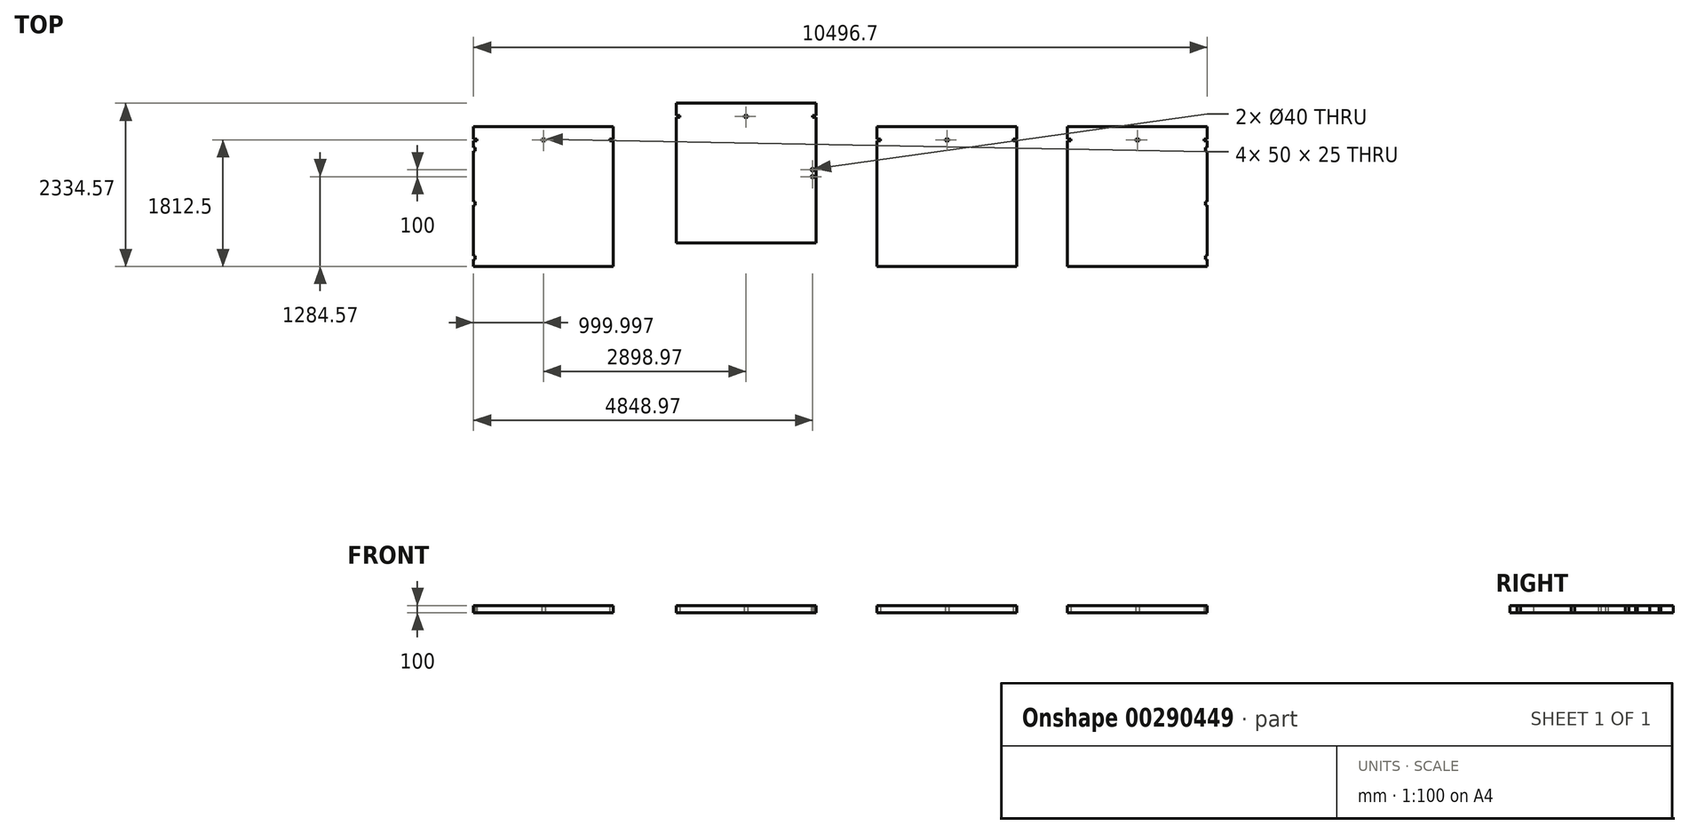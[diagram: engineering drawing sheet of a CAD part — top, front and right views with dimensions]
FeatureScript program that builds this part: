
annotation { "Feature Type Name" : "Feature", "Feature Type Description" : "" }
export const myFeature = defineFeature(function(context is Context, id is Id, definition is map)
    precondition{}
    {
        {
            var Q0;
            Q0=qCreatedBy(makeId("Top.planeOp"),FACE);
            var sketch = newSketch(context, id + "F0", { "sketchPlane" : qUnion([Q0])});
            skLineSegment(sketch, "E0.bottom", {"start": v(0, 0) * mm, "end": v(2000, 0) * mm});
            skLineSegment(sketch, "E0.top", {"start": v(0, -2000) * mm, "end": v(2000, -2000) * mm});
            skLineSegment(sketch, "E1.bottom", {"start": v(0, -200) * mm, "end": v(50, -200) * mm});
            skLineSegment(sketch, "E2.bottom", {"start": v(2000, -200) * mm, "end": v(1950, -200) * mm});
            skLineSegment(sketch, "E3.bottom", {"start": v(975, -200) * mm, "end": v(1025, -200) * mm});
            skLineSegment(sketch, "E4.bottom", {"start": v(50, -200) * mm, "end": v(0, -200) * mm});
            skLineSegment(sketch, "E4.top", {"start": v(50, -175) * mm, "end": v(0, -175) * mm});
            skLineSegment(sketch, "E4.left", {"start": v(50, -200) * mm, "end": v(50, -175) * mm});
            skLineSegment(sketch, "E5", {"start": v(0, 0) * mm, "end": v(0, -175) * mm});
            skLineSegment(sketch, "E6", {"start": v(0, -200) * mm, "end": v(0, -2000) * mm});
            skLineSegment(sketch, "E7.top", {"start": v(975, -175) * mm, "end": v(1025, -175) * mm});
            skLineSegment(sketch, "E7.left", {"start": v(975, -200) * mm, "end": v(975, -175) * mm});
            skLineSegment(sketch, "E7.right", {"start": v(1025, -200) * mm, "end": v(1025, -175) * mm});
            skLineSegment(sketch, "E8.bottom", {"start": v(1950, -200) * mm, "end": v(2000, -200) * mm});
            skLineSegment(sketch, "E8.top", {"start": v(1950, -175) * mm, "end": v(2000, -175) * mm});
            skLineSegment(sketch, "E8.left", {"start": v(1950, -200) * mm, "end": v(1950, -175) * mm});
            skLineSegment(sketch, "E9", {"start": v(2000, -175) * mm, "end": v(2000, 0) * mm});
            skLineSegment(sketch, "E10", {"start": v(2000, -200) * mm, "end": v(2000, -2000) * mm});
            skSolve(sketch);
        }
        {
            var Q0;
            Q0=makeQuery(id+"F0.imprint","IMPRINT",FACE,{"disambiguationData":[TD([[makeQuery(id+"F0.imprint","IMPRINT",EDGE,{"derivedFrom":sQuery(id+"F0.wireOp",EDGE,"E0.bottom")}),-1.0]])]});
            extrude(context, id + "F1", {"entities" : qUnion([Q0]), "depth" : 100 * mm});
        }
        {
            var Q0;
            Q0=qCreatedBy(makeId("Top.planeOp"),FACE);
            var sketch = newSketch(context, id + "F2", { "sketchPlane" : qUnion([Q0])});
            skLineSegment(sketch, "E11.bottom", {"start": v(-2872.43, 334.57) * mm, "end": v(-872.43, 334.57) * mm});
            skLineSegment(sketch, "E12.bottom", {"start": v(-2872.43, 134.57) * mm, "end": v(-2822.43, 134.57) * mm});
            skLineSegment(sketch, "E13.bottom", {"start": v(-1897.43, 134.57) * mm, "end": v(-1847.43, 134.57) * mm});
            skLineSegment(sketch, "E14.bottom", {"start": v(-872.43, 134.57) * mm, "end": v(-922.43, 134.57) * mm});
            skLineSegment(sketch, "E15.bottom", {"start": v(-2822.43, 134.57) * mm, "end": v(-2872.43, 134.57) * mm});
            skLineSegment(sketch, "E15.top", {"start": v(-2822.43, 159.57) * mm, "end": v(-2872.43, 159.57) * mm});
            skLineSegment(sketch, "E15.left", {"start": v(-2822.43, 134.57) * mm, "end": v(-2822.43, 159.57) * mm});
            skLineSegment(sketch, "E16.top", {"start": v(-1897.43, 159.57) * mm, "end": v(-1847.43, 159.57) * mm});
            skLineSegment(sketch, "E16.left", {"start": v(-1897.43, 134.57) * mm, "end": v(-1897.43, 159.57) * mm});
            skLineSegment(sketch, "E16.right", {"start": v(-1847.43, 134.57) * mm, "end": v(-1847.43, 159.57) * mm});
            skLineSegment(sketch, "E17.bottom", {"start": v(-922.43, 134.57) * mm, "end": v(-872.43, 134.57) * mm});
            skLineSegment(sketch, "E17.top", {"start": v(-922.43, 159.57) * mm, "end": v(-872.43, 159.57) * mm});
            skLineSegment(sketch, "E17.left", {"start": v(-922.43, 134.57) * mm, "end": v(-922.43, 159.57) * mm});
            skLineSegment(sketch, "E18", {"start": v(-872.43, 334.57) * mm, "end": v(-872.43, 159.57) * mm});
            skLineSegment(sketch, "E19", {"start": v(-872.43, 134.57) * mm, "end": v(-872.43, -1665.43) * mm});
            skLineSegment(sketch, "E20", {"start": v(-2872.43, 159.57) * mm, "end": v(-2872.43, 334.57) * mm});
            skLineSegment(sketch, "E21", {"start": v(-2872.43, 134.57) * mm, "end": v(-2872.43, -1665.43) * mm});
            skLineSegment(sketch, "E22", {"start": v(-2872.43, -1665.43) * mm, "end": v(-872.43, -1665.43) * mm});
            skLineSegment(sketch, "E23", {"start": v(-872.43, -1665.43) * mm, "end": v(-972.43, -1665.43) * mm});
            skCircle(sketch, "E24", {"center": v(-922.43, -615.43) * mm, "radius": 20 * mm});
            skCircle(sketch, "E25.MirrorC", {"center": v(-922.43, -715.43) * mm, "radius": 20 * mm});
            skSolve(sketch);
        }
        {
            var Q0;
            Q0=makeQuery(id+"F2.imprint","IMPRINT",FACE,{"disambiguationData":[TD([[makeQuery(id+"F2.imprint","IMPRINT",EDGE,{"derivedFrom":sQuery(id+"F2.wireOp",EDGE,"E11.bottom")}),-1.0]])]});
            extrude(context, id + "F3", {"entities" : qUnion([Q0]), "depth" : 100 * mm});
        }
        {
            var Q0;
            Q0=qCreatedBy(makeId("Top.planeOp"),FACE);
            var sketch = newSketch(context, id + "F4", { "sketchPlane" : qUnion([Q0])});
            skLineSegment(sketch, "E26", {"start": v(2725.3, -2000) * mm, "end": v(4725.3, -2000) * mm});
            skLineSegment(sketch, "E27", {"start": v(4725.3, -2000) * mm, "end": v(4725.3, -1900) * mm});
            skLineSegment(sketch, "E28", {"start": v(4725.3, -1900) * mm, "end": v(4700.3, -1900) * mm});
            skLineSegment(sketch, "E29", {"start": v(4700.3, -1900) * mm, "end": v(4700.3, -1850) * mm});
            skLineSegment(sketch, "E30", {"start": v(4700.3, -1850) * mm, "end": v(4725.3, -1850) * mm});
            skLineSegment(sketch, "E31", {"start": v(4725.3, -1850) * mm, "end": v(4725.3, -1125) * mm});
            skLineSegment(sketch, "E32", {"start": v(4725.3, -1125) * mm, "end": v(4700.3, -1125) * mm});
            skLineSegment(sketch, "E33", {"start": v(4700.3, -1125) * mm, "end": v(4700.3, -1075) * mm});
            skLineSegment(sketch, "E34", {"start": v(4700.3, -1075) * mm, "end": v(4725.3, -1075) * mm});
            skLineSegment(sketch, "E35", {"start": v(4725.3, -1075) * mm, "end": v(4725.3, -350) * mm});
            skLineSegment(sketch, "E36", {"start": v(4725.3, -350) * mm, "end": v(4700.3, -350) * mm});
            skLineSegment(sketch, "E37", {"start": v(4700.3, -350) * mm, "end": v(4700.3, -300) * mm});
            skLineSegment(sketch, "E38", {"start": v(4700.3, -300) * mm, "end": v(4725.3, -300) * mm});
            skLineSegment(sketch, "E39", {"start": v(4725.3, -300) * mm, "end": v(4725.3, -200) * mm});
            skLineSegment(sketch, "E40", {"start": v(4725.3, -200) * mm, "end": v(4675.3, -200) * mm});
            skLineSegment(sketch, "E41", {"start": v(4675.3, -200) * mm, "end": v(4675.3, -175) * mm});
            skLineSegment(sketch, "E42", {"start": v(4675.3, -175) * mm, "end": v(4725.3, -175) * mm});
            skLineSegment(sketch, "E43", {"start": v(4725.3, -175) * mm, "end": v(4725.3, 0) * mm});
            skLineSegment(sketch, "E44", {"start": v(4725.3, 0) * mm, "end": v(2725.3, 0) * mm});
            skLineSegment(sketch, "E45", {"start": v(3750.3, -175) * mm, "end": v(3750.3, -200) * mm});
            skLineSegment(sketch, "E46", {"start": v(3750.3, -200) * mm, "end": v(3700.3, -200) * mm});
            skLineSegment(sketch, "E47", {"start": v(3700.3, -200) * mm, "end": v(3700.3, -175) * mm});
            skLineSegment(sketch, "E48", {"start": v(3700.3, -175) * mm, "end": v(3750.3, -175) * mm});
            skLineSegment(sketch, "E49", {"start": v(2775.3, -175) * mm, "end": v(2775.3, -200) * mm});
            skLineSegment(sketch, "E50", {"start": v(2775.3, -200) * mm, "end": v(2725.3, -200) * mm});
            skLineSegment(sketch, "E51", {"start": v(2725.3, -175) * mm, "end": v(2775.3, -175) * mm});
            skLineSegment(sketch, "E52", {"start": v(2725.3, -2000) * mm, "end": v(2725.3, -200) * mm});
            skLineSegment(sketch, "E53", {"start": v(2725.3, -175) * mm, "end": v(2725.3, 0) * mm});
            skLineSegment(sketch, "E54", {"start": v(-523.05, 368.16) * mm, "end": v(-523.05, -2315.85) * mm});
            skLineSegment(sketch, "E55.MirrorCS", {"start": v(-3821.4, -175) * mm, "end": v(-3821.4, -200) * mm});
            skLineSegment(sketch, "E56.MirrorCS", {"start": v(-5721.4, -200) * mm, "end": v(-5721.4, -175) * mm});
            skLineSegment(sketch, "E57.MirrorCS", {"start": v(-3821.4, -200) * mm, "end": v(-3771.4, -200) * mm});
            skLineSegment(sketch, "E58.MirrorCS", {"start": v(-5771.4, -350) * mm, "end": v(-5746.4, -350) * mm});
            skLineSegment(sketch, "E59.MirrorCS", {"start": v(-3771.4, -175) * mm, "end": v(-3821.4, -175) * mm});
            skLineSegment(sketch, "E60.MirrorCS", {"start": v(-5746.4, -1900) * mm, "end": v(-5746.4, -1850) * mm});
            skLineSegment(sketch, "E61.MirrorCS", {"start": v(-5771.4, -200) * mm, "end": v(-5721.4, -200) * mm});
            skLineSegment(sketch, "E62.MirrorCS", {"start": v(-5771.4, -1125) * mm, "end": v(-5746.4, -1125) * mm});
            skLineSegment(sketch, "E63.MirrorCS", {"start": v(-5746.4, -1125) * mm, "end": v(-5746.4, -1075) * mm});
            skLineSegment(sketch, "E64.MirrorCS", {"start": v(-4746.4, -200) * mm, "end": v(-4746.4, -175) * mm});
            skLineSegment(sketch, "E65.MirrorCS", {"start": v(-5746.4, -1850) * mm, "end": v(-5771.4, -1850) * mm});
            skLineSegment(sketch, "E66.MirrorCS", {"start": v(-5746.4, -1075) * mm, "end": v(-5771.4, -1075) * mm});
            skLineSegment(sketch, "E67.MirrorCS", {"start": v(-5746.4, -350) * mm, "end": v(-5746.4, -300) * mm});
            skLineSegment(sketch, "E68.MirrorCS", {"start": v(-5746.4, -300) * mm, "end": v(-5771.4, -300) * mm});
            skLineSegment(sketch, "E69.MirrorCS", {"start": v(-5771.4, -300) * mm, "end": v(-5771.4, -200) * mm});
            skLineSegment(sketch, "E70.MirrorCS", {"start": v(-5721.4, -175) * mm, "end": v(-5771.4, -175) * mm});
            skLineSegment(sketch, "E71.MirrorCS", {"start": v(-4796.4, -175) * mm, "end": v(-4796.4, -200) * mm});
            skLineSegment(sketch, "E72.MirrorCS", {"start": v(-5771.4, -2000) * mm, "end": v(-5771.4, -1900) * mm});
            skLineSegment(sketch, "E73.MirrorCS", {"start": v(-5771.4, -1900) * mm, "end": v(-5746.4, -1900) * mm});
            skLineSegment(sketch, "E74.MirrorCS", {"start": v(-4746.4, -175) * mm, "end": v(-4796.4, -175) * mm});
            skLineSegment(sketch, "E75.MirrorCS", {"start": v(-4796.4, -200) * mm, "end": v(-4746.4, -200) * mm});
            skLineSegment(sketch, "E76.MirrorCS", {"start": v(-5771.4, -175) * mm, "end": v(-5771.4, 0) * mm});
            skLineSegment(sketch, "E77.MirrorCS", {"start": v(-3771.4, -175) * mm, "end": v(-3771.4, 0) * mm});
            skLineSegment(sketch, "E78.MirrorCS", {"start": v(-3771.4, -2000) * mm, "end": v(-3771.4, -200) * mm});
            skLineSegment(sketch, "E79.MirrorCS", {"start": v(-5771.4, -1075) * mm, "end": v(-5771.4, -350) * mm});
            skLineSegment(sketch, "E80.MirrorCS", {"start": v(-5771.4, 0) * mm, "end": v(-3771.4, 0) * mm});
            skLineSegment(sketch, "E81.MirrorCS", {"start": v(-5771.4, -1850) * mm, "end": v(-5771.4, -1125) * mm});
            skLineSegment(sketch, "E82.MirrorCS", {"start": v(-3771.4, -2000) * mm, "end": v(-5771.4, -2000) * mm});
            skSolve(sketch);
        }
        {
            var Q0;
            Q0=makeQuery(id+"F4.imprint","IMPRINT",FACE,{"disambiguationData":[TD([[makeQuery(id+"F4.imprint","IMPRINT",EDGE,{"derivedFrom":sQuery(id+"F4.wireOp",EDGE,"E55.MirrorCS")}),-1.0]])]});
            var Q1;
            Q1=makeQuery(id+"F4.imprint","IMPRINT",FACE,{"disambiguationData":[TD([[makeQuery(id+"F4.imprint","IMPRINT",EDGE,{"derivedFrom":sQuery(id+"F4.wireOp",EDGE,"E26")}),1.0]])]});
            extrude(context, id + "F5", {"entities" : qUnion([Q0, Q1]), "depth" : 100 * mm});
        }
    });
